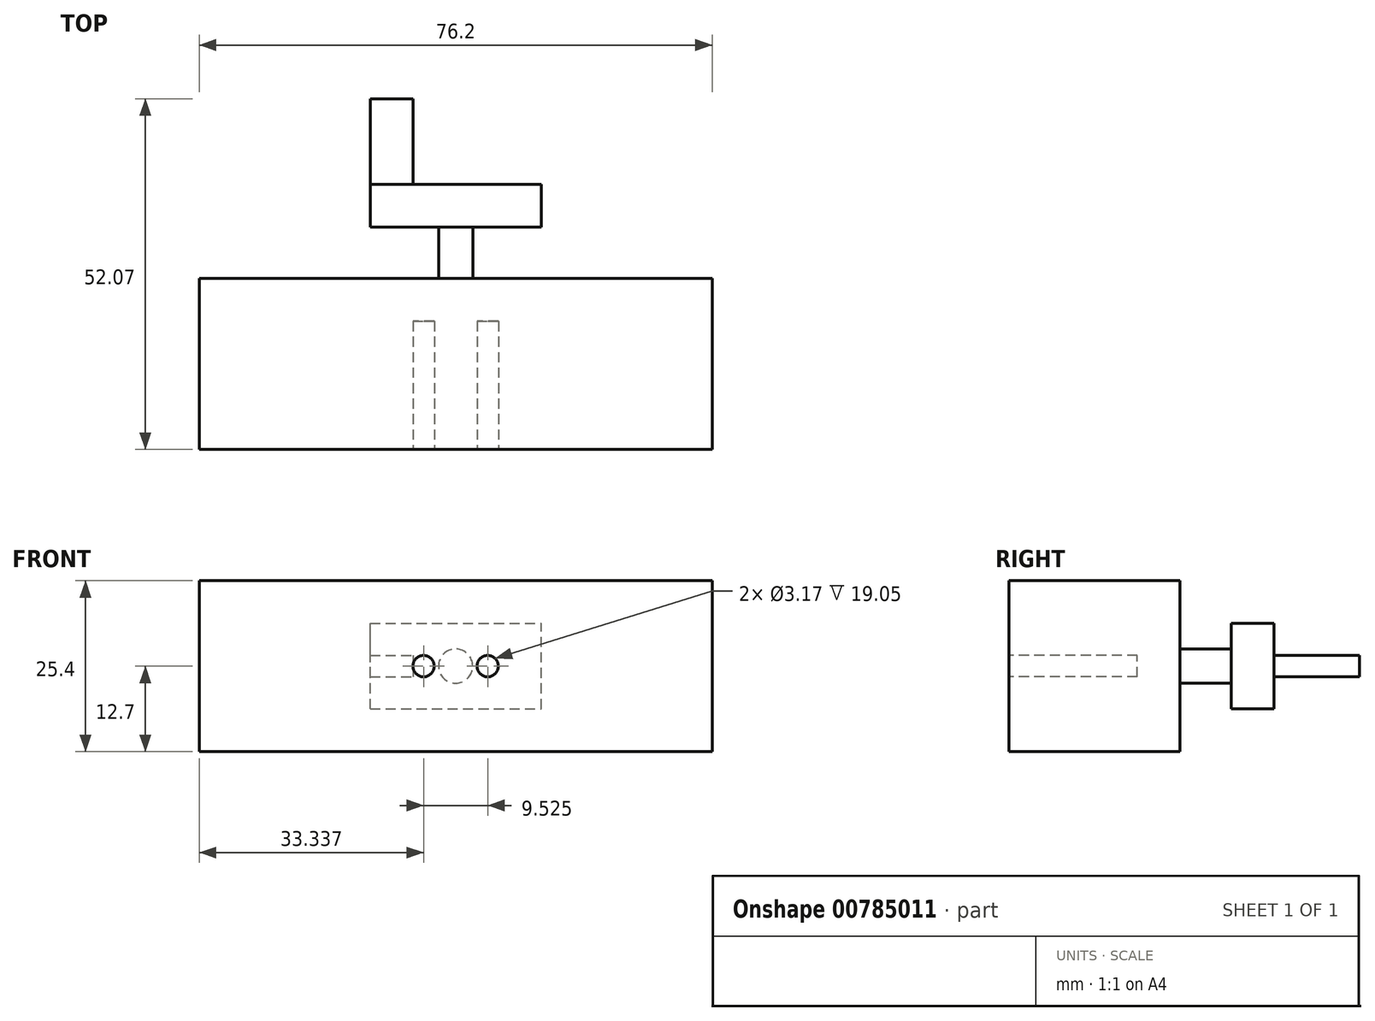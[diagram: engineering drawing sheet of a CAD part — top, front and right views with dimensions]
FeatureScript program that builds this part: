
annotation { "Feature Type Name" : "Feature", "Feature Type Description" : "" }
export const myFeature = defineFeature(function(context is Context, id is Id, definition is map)
    precondition{}
    {
        {
            var Q0;
            Q0=qCreatedBy(makeId("Front.planeOp"),FACE);
            var sketch = newSketch(context, id + "F0", { "sketchPlane" : qUnion([Q0])});
            skLineSegment(sketch, "E0.bottom", {"start": v(38.1, -12.7) * mm, "end": v(-38.1, -12.7) * mm});
            skLineSegment(sketch, "E0.top", {"start": v(38.1, 12.7) * mm, "end": v(-38.1, 12.7) * mm});
            skLineSegment(sketch, "E0.left", {"start": v(38.1, -12.7) * mm, "end": v(38.1, 12.7) * mm});
            skLineSegment(sketch, "E0.right", {"start": v(-38.1, -12.7) * mm, "end": v(-38.1, 12.7) * mm});
            skPoint(sketch, "E0.middle", {"position": v(0, 0) * mm});
            skCircle(sketch, "E1", {"center": v(4.76, 0) * mm, "radius": 1.59 * mm});
            skCircle(sketch, "E2", {"center": v(-4.76, 0) * mm, "radius": 1.59 * mm});
            skSolve(sketch);
        }
        {
            var Q0;
            Q0=qSketchRegion(id+"F0",true);
            var Q1;
            Q1=makeQuery(id+"F0.imprint","IMPRINT",FACE,{"disambiguationData":[TD([[makeQuery(id+"F0.imprint","IMPRINT",EDGE,{"derivedFrom":sQuery(id+"F0.wireOp",EDGE,"E2")}),1.0]])]});
            var Q2;
            Q2=makeQuery(id+"F0.imprint","IMPRINT",FACE,{"disambiguationData":[TD([[makeQuery(id+"F0.imprint","IMPRINT",EDGE,{"derivedFrom":sQuery(id+"F0.wireOp",EDGE,"E1")}),1.0]])]});
            extrude(context, id + "F1", {"entities" : qUnion([Q0, Q1, Q2]), "oppositeDirection" : true, "depth" : 25.4 * mm, "offsetDistance" : 25.4 * mm});
        }
        {
            var Q0;
            Q0=makeQuery(id+"F1.opExtrude","CAP_FACE",FACE,{"disambiguationData":[OSD([sQuery(id+"F0.wireOp",EDGE,"E0.bottom"),sQuery(id+"F0.wireOp",EDGE,"E0.top"),sQuery(id+"F0.wireOp",EDGE,"E0.left"),sQuery(id+"F0.wireOp",EDGE,"E0.right")])],"isStart":false});
            var sketch = newSketch(context, id + "F2", { "sketchPlane" : qUnion([Q0])});
            skCircle(sketch, "E3", {"center": v(0, 0) * mm, "radius": 2.54 * mm});
            skSolve(sketch);
        }
        {
            var Q0;
            Q0=makeQuery(id+"F2.imprint","IMPRINT",FACE,{"disambiguationData":[TD([[makeQuery(id+"F2.imprint","IMPRINT",EDGE,{"derivedFrom":sQuery(id+"F2.wireOp",EDGE,"E3")}),1.0]])]});
            extrude(context, id + "F3", {"entities" : qUnion([Q0]), "operationType" : NewBodyOperationType.ADD, "depth" : 7.62 * mm, "offsetDistance" : 25.4 * mm});
        }
        {
            var Q0;
            Q0=makeQuery(id+"F3.opExtrude","CAP_FACE",FACE,{"disambiguationData":[OSD([sQuery(id+"F2.wireOp",EDGE,"E3")])],"isStart":false});
            var sketch = newSketch(context, id + "F4", { "sketchPlane" : qUnion([Q0])});
            skLineSegment(sketch, "E4.bottom", {"start": v(12.7, -6.35) * mm, "end": v(-12.7, -6.35) * mm});
            skLineSegment(sketch, "E4.top", {"start": v(12.7, 6.35) * mm, "end": v(-12.7, 6.35) * mm});
            skLineSegment(sketch, "E4.left", {"start": v(12.7, -6.35) * mm, "end": v(12.7, 6.35) * mm});
            skLineSegment(sketch, "E4.right", {"start": v(-12.7, -6.35) * mm, "end": v(-12.7, 6.35) * mm});
            skPoint(sketch, "E4.middle", {"position": v(0, 0) * mm});
            skSolve(sketch);
        }
        {
            var Q0;
            Q0=qSketchRegion(id+"F4",true);
            extrude(context, id + "F5", {"entities" : qUnion([Q0]), "operationType" : NewBodyOperationType.ADD, "depth" : 6.35 * mm, "offsetDistance" : 25.4 * mm});
        }
        {
            var Q0;
            Q0=makeQuery(id+"F5.opExtrude","CAP_FACE",FACE,{"disambiguationData":[OSD([sQuery(id+"F4.wireOp",EDGE,"E4.bottom"),sQuery(id+"F4.wireOp",EDGE,"E4.top"),sQuery(id+"F4.wireOp",EDGE,"E4.left"),sQuery(id+"F4.wireOp",EDGE,"E4.right")])],"isStart":false});
            var sketch = newSketch(context, id + "F6", { "sketchPlane" : qUnion([Q0])});
            skLineSegment(sketch, "E5.bottom", {"start": v(12.7, 1.59) * mm, "end": v(6.35, 1.59) * mm});
            skLineSegment(sketch, "E5.top", {"start": v(12.7, -1.59) * mm, "end": v(6.35, -1.59) * mm});
            skLineSegment(sketch, "E5.left", {"start": v(12.7, 1.59) * mm, "end": v(12.7, -1.59) * mm});
            skLineSegment(sketch, "E5.right", {"start": v(6.35, 1.59) * mm, "end": v(6.35, -1.59) * mm});
            skSolve(sketch);
        }
        {
            var Q0;
            Q0=makeQuery(id+"F6.imprint","IMPRINT",FACE,{"disambiguationData":[TD([[makeQuery(id+"F6.imprint","IMPRINT",EDGE,{"derivedFrom":sQuery(id+"F6.wireOp",EDGE,"E5.bottom")}),1.0]])]});
            extrude(context, id + "F7", {"entities" : qUnion([Q0]), "operationType" : NewBodyOperationType.ADD, "depth" : 12.7 * mm, "offsetDistance" : 25.4 * mm});
        }
        {
            var Q0;
            Q0=makeQuery(id+"F0.imprint","IMPRINT",FACE,{"disambiguationData":[TD([[makeQuery(id+"F0.imprint","IMPRINT",EDGE,{"derivedFrom":sQuery(id+"F0.wireOp",EDGE,"E2")}),1.0]])]});
            var Q1;
            Q1=makeQuery(id+"F0.imprint","IMPRINT",FACE,{"disambiguationData":[TD([[makeQuery(id+"F0.imprint","IMPRINT",EDGE,{"derivedFrom":sQuery(id+"F0.wireOp",EDGE,"E1")}),1.0]])]});
            extrude(context, id + "F8", {"entities" : qUnion([Q0, Q1]), "operationType" : NewBodyOperationType.REMOVE, "oppositeDirection" : true, "depth" : 19.05 * mm, "offsetDistance" : 25.4 * mm});
        }
    });
